FCSTD DOCUMENT  (FreeCAD 1.0R39319 (Git))
Label: Assy_Stack_Module_Tee_Cam
License: All rights reserved
LicenseURL: https://en.wikipedia.org/wiki/All_rights_reserved
objects: App::DocumentObjectGroup×3, App::Link×2, PartDesign::CoordinateSystem×1, App::FeaturePython×1, App::Part×1, TechDraw::DrawSVGTemplate×1, TechDraw::DrawProjGroupItem×1, TechDraw::DrawPage×1
note: 1 computed .brp shape members not serialized (recipe doc carries the construction recipe); baked Part::Feature solids carry a one-line shape summary decoded from their .brp
EXTERNAL_REF file=Assy_Stack_Module.FCStd obj=LCS_Origin
EXTERNAL_REF file=Assy_Stack_Module.FCStd obj=Assembly
EXTERNAL_REF file=Assy_Tee_Cam.FCStd obj=LCS_Origin
EXTERNAL_REF file=Assy_Tee_Cam.FCStd obj=Assembly

FEATURE [App::DocumentObjectGroup] Parts
FEATURE [PartDesign::CoordinateSystem] LCS_Origin
  AttacherType = Attacher::AttachEngine3D
  AttachmentSupport = -> [X_Axis]
  MapMode = 2
FEATURE [App::DocumentObjectGroup] Constraints
FEATURE [App::FeaturePython] Variables  # WARN: FeaturePython — macro-defined, semantics opaque (R4)
  Type = App::PropertyContainer
FEATURE [App::DocumentObjectGroup] Configurations
FEATURE [App::Link] Assy_Stack_Module
  AttachedBy = #LCS_Origin
  AttachedTo = Parent Assembly#LCS_Origin
  LinkedObject = -> <external Assy_Stack_Module.FCStd>#Assembly
  SolverId = Asm4EE
  expr: Placement = LCS_Origin.Placement * AttachmentOffset * Assy_Stack_Module#LCS_Origin.Placement ^ -1
FEATURE [App::Link] Assy_Tee_Cam
  AttachedBy = #LCS_Origin
  AttachedTo = Assy_Stack_Module#LCS_Origin
  AttachmentOffset = pos=(0,50,-41.75) rot=(-0.57735,0.57735,-0.57735;4.18879rad)
  LinkPlacement = pos=(0,50,-41.75) rot=(-0.57735,0.57735,-0.57735;4.18879rad)
  LinkedObject = -> <external Assy_Tee_Cam.FCStd>#Assembly
  Placement = pos=(0,50,-41.75) rot=(-0.57735,0.57735,-0.57735;4.18879rad)
  SolverId = Asm4EE
  expr: Placement = Assy_Stack_Module.Placement * Assy_Stack_Module#LCS_Origin.Placement * AttachmentOffset * Assy_Tee_Cam#LCS_Origin.Placement ^ -1
FEATURE [App::Part] Assembly  label="Assy_Stack_Module_Tee_Cam"
  AssemblyType = Part::Link
  Group = -> [LCS_Origin,Constraints,Variables,Configurations,Assy_Stack_Module,Assy_Tee_Cam]
  Origin = -> Origin
  Type = Assembly
FEATURE [TechDraw::DrawSVGTemplate] Template
  Height = 210
  Orientation = 1
  Template = C:/Program Files/FreeCAD 1.0/data/Mod/TechDraw/Templates/Default_Template_A4_Landscape.svg
  Width = 297
FEATURE [TechDraw::DrawProjGroupItem] View
  CoarseView = false
  Direction = (-0.57735,0.57735,-0.577351)
  Focus = 100
  HardHidden = false
  IsoCount = 0
  IsoHidden = false
  IsoVisible = false
  LockPosition = false
  Perspective = false
  Rotation = 0
  RotationVector = (1,0,0)
  ScaleType = 0
  ScrubCount = 1
  SeamHidden = false
  SeamVisible = false
  SmoothHidden = false
  SmoothVisible = true
  Source = -> [Assembly]
  Type = 0
  X = 148.5
  XDirection = (0.707107,0.707107,0)
  Y = 105
FEATURE [TechDraw::DrawPage] Page
  KeepUpdated = true
  NextBalloonIndex = 1
  ProjectionType = 0
  Template = -> Template
  Views = -> [View]

RESOLVED EXTERNAL PARTS (link-assembly join: the EXTERNAL_REF files above that resolve inside this repo's crawl, each included once):
---- part Assy_Stack_Module.FCStd = doc fcstd_b85c8f13e317 ----
FCSTD DOCUMENT  (FreeCAD 1.0R39319 (Git))
Label: Assy_Stack_Module
License: All rights reserved
LicenseURL: https://en.wikipedia.org/wiki/All_rights_reserved
objects: App::Link×5, Part::FeaturePython×4, App::DocumentObjectGroup×3, PartDesign::CoordinateSystem×1, App::FeaturePython×1, App::Part×1
note: 5 computed .brp shape members not serialized (recipe doc carries the construction recipe); baked Part::Feature solids carry a one-line shape summary decoded from their .brp
EXTERNAL_REF file=../../Part/Print/Stack_Module.FCStd obj=screen_ref
EXTERNAL_REF file=../../Part/Print/Stack_Module.FCStd obj=Part
EXTERNAL_REF file=../../Part/Print/Spacer.FCStd obj=LCS_1
EXTERNAL_REF file=../../Part/Print/Stack_Module.FCStd obj=spacer_att_1
EXTERNAL_REF file=../../Part/Print/Spacer.FCStd obj=Part
EXTERNAL_REF file=../../Part/Print/Stack_Module.FCStd obj=spacer_att_2
EXTERNAL_REF file=../../Part/Print/Stack_Module.FCStd obj=spacer_att_3
EXTERNAL_REF file=../../Part/Print/Stack_Module.FCStd obj=spacer_att_4

FEATURE [App::DocumentObjectGroup] Parts
FEATURE [PartDesign::CoordinateSystem] LCS_Origin
  AttacherType = Attacher::AttachEngine3D
  AttachmentSupport = -> [X_Axis]
  MapMode = 2
FEATURE [App::DocumentObjectGroup] Constraints
FEATURE [App::FeaturePython] Variables  # WARN: FeaturePython — macro-defined, semantics opaque (R4)
  Type = App::PropertyContainer
FEATURE [App::DocumentObjectGroup] Configurations
FEATURE [App::Link] Stack_Module
  AttachedBy = #screen_ref
  AttachedTo = Parent Assembly#LCS_Origin
  LinkPlacement = pos=(19.9856,50,3) rot=(0.57735,0.57735,0.57735;2.0944rad)
  LinkedObject = -> <external ../../Part/Print/Stack_Module.FCStd>#Part
  Placement = pos=(19.9856,50,3) rot=(0.57735,0.57735,0.57735;2.0944rad)
  SolverId = Asm4EE
  expr: Placement = LCS_Origin.Placement * AttachmentOffset * Stack_Module#screen_ref.Placement ^ -1
FEATURE [App::Link] Spacer
  AttachedBy = #LCS_1
  AttachedTo = Stack_Module#spacer_att_1
  LinkPlacement = pos=(-33.5144,116.5,-79.5) rot=(0.707107,0.707107,0;3.14159rad)
  LinkedObject = -> <external ../../Part/Print/Spacer.FCStd>#Part
  Placement = pos=(-33.5144,116.5,-79.5) rot=(0.707107,0.707107,0;3.14159rad)
  SolverId = Asm4EE
  expr: Placement = Stack_Module.Placement * Stack_Module#spacer_att_1.Placement * AttachmentOffset * Spacer#LCS_1.Placement ^ -1
FEATURE [App::Link] Spacer001
  AttachedBy = #LCS_1
  AttachedTo = Stack_Module#spacer_att_2
  LinkPlacement = pos=(82.4856,113.5,-79.5) rot=(0.707107,0.707107,0;3.14159rad)
  LinkedObject = -> <external ../../Part/Print/Spacer.FCStd>#Part
  Placement = pos=(82.4856,113.5,-79.5) rot=(0.707107,0.707107,0;3.14159rad)
  SolverId = Asm4EE
  expr: Placement = Stack_Module.Placement * Stack_Module#spacer_att_2.Placement * AttachmentOffset * Spacer#LCS_1.Placement ^ -1
FEATURE [App::Link] Spacer002
  AttachedBy = #LCS_1
  AttachedTo = Stack_Module#spacer_att_3
  AttachmentOffset = pos=(0,0,0) rot=(0,1,0;3.14159rad)
  LinkPlacement = pos=(-33.5144,-16.5,-79.5) rot=(0.707107,-0.707107,0;3.14159rad)
  LinkedObject = -> <external ../../Part/Print/Spacer.FCStd>#Part
  Placement = pos=(-33.5144,-16.5,-79.5) rot=(0.707107,-0.707107,0;3.14159rad)
  SolverId = Asm4EE
  expr: Placement = Stack_Module.Placement * Stack_Module#spacer_att_3.Placement * AttachmentOffset * Spacer#LCS_1.Placement ^ -1
FEATURE [App::Link] Spacer003
  AttachedBy = #LCS_1
  AttachedTo = Stack_Module#spacer_att_4
  AttachmentOffset = pos=(0,0,0) rot=(0,1,0;3.14159rad)
  LinkPlacement = pos=(82.4856,-13.5,-79.5) rot=(0.707107,-0.707107,0;3.14159rad)
  LinkedObject = -> <external ../../Part/Print/Spacer.FCStd>#Part
  Placement = pos=(82.4856,-13.5,-79.5) rot=(0.707107,-0.707107,0;3.14159rad)
  SolverId = Asm4EE
  expr: Placement = Stack_Module.Placement * Stack_Module#spacer_att_4.Placement * AttachmentOffset * Spacer#LCS_1.Placement ^ -1
FEATURE [Part::FeaturePython] Screw  label="M5x10-Screw"  # WARN: FeaturePython — macro-defined, semantics opaque (R4)
  BaseObject = -> Stack_Module [Body.Mirrored.Edge531]
  Diameter = 3
  Invert = true
  LeftHanded = false
  Length = 1
  LengthCustom = 10
  MatchOuter = false
  OffsetAngle = 0
  Placement = pos=(-31.0144,2.23e-14,-3) rot=(0.830469,-0.557065,0;3.14159rad)
  Thread = false
  Type = 86
FEATURE [Part::FeaturePython] Screw001  label="M5x10-Screw007"  # WARN: FeaturePython — macro-defined, semantics opaque (R4)
  BaseObject = -> Stack_Module [Body.Mirrored.Edge537]
  Diameter = 3
  Invert = true
  LeftHanded = false
  Length = 1
  LengthCustom = 10
  MatchOuter = false
  OffsetAngle = 0
  Placement = pos=(35.9856,8.1e-15,-3) rot=(0.830469,-0.557065,0;3.14159rad)
  Thread = false
  Type = 86
FEATURE [Part::FeaturePython] Screw002  label="M5x10-Screw008"  # WARN: FeaturePython — macro-defined, semantics opaque (R4)
  BaseObject = -> Stack_Module [Body.Mirrored.Edge265]
  Diameter = 3
  Invert = false
  LeftHanded = false
  Length = 1
  LengthCustom = 10
  MatchOuter = false
  OffsetAngle = 0
  Placement = pos=(35.9856,100,-3) rot=(-1,0,0;3.14159rad)
  Thread = false
  Type = 86
FEATURE [Part::FeaturePython] Screw003  label="M5x10-Screw009"  # WARN: FeaturePython — macro-defined, semantics opaque (R4)
  BaseObject = -> Stack_Module [Body.Mirrored.Edge258]
  Diameter = 3
  Invert = false
  LeftHanded = false
  Length = 1
  LengthCustom = 10
  MatchOuter = false
  OffsetAngle = 0
  Placement = pos=(-31.0144,100,-3) rot=(-1,0,0;3.14159rad)
  Thread = false
  Type = 86
FEATURE [App::Part] Assembly  label="Assy_Stack_Module"
  AssemblyType = Part::Link
  Group = -> [LCS_Origin,Constraints,Variables,Configurations,Stack_Module,Spacer,Spacer001,Spacer002,Spacer003,Screw,Screw001,Screw002,Screw003]
  Origin = -> Origin
  Type = Assembly
---- part Assy_Tee_Cam.FCStd = doc fcstd_2765aa89e358 ----
FCSTD DOCUMENT  (FreeCAD 1.0R39319 (Git))
Label: Assy_Tee_Cam
License: All rights reserved
LicenseURL: https://en.wikipedia.org/wiki/All_rights_reserved
objects: App::DocumentObjectGroup×3, App::Link×3, PartDesign::CoordinateSystem×1, App::FeaturePython×1, App::Part×1
note: 1 computed .brp shape members not serialized (recipe doc carries the construction recipe); baked Part::Feature solids carry a one-line shape summary decoded from their .brp
EXTERNAL_REF file=Assy_Camera_Eyeball.FCStd obj=LCS_Origin
EXTERNAL_REF file=Assy_Camera_Eyeball.FCStd obj=Assembly
EXTERNAL_REF file=Assy_EyeScreen.FCStd obj=LCS_Origin
EXTERNAL_REF file=Assy_EyeScreen.FCStd obj=Assembly
EXTERNAL_REF file=Assy_EyeScreen_Clamp.FCStd obj=LCS_Origin
EXTERNAL_REF file=Assy_EyeScreen_Clamp.FCStd obj=Assembly

FEATURE [App::DocumentObjectGroup] Parts
FEATURE [PartDesign::CoordinateSystem] LCS_Origin
  AttacherType = Attacher::AttachEngine3D
  AttachmentSupport = -> [X_Axis]
  MapMode = 2
FEATURE [App::DocumentObjectGroup] Constraints
FEATURE [App::FeaturePython] Variables  # WARN: FeaturePython — macro-defined, semantics opaque (R4)
  Type = App::PropertyContainer
FEATURE [App::DocumentObjectGroup] Configurations
FEATURE [App::Link] Assy_Camera_Eyeball
  AttachedBy = #LCS_Origin
  AttachedTo = Parent Assembly#LCS_Origin
  LinkedObject = -> <external Assy_Camera_Eyeball.FCStd>#Assembly
  SolverId = Asm4EE
  expr: Placement = LCS_Origin.Placement * AttachmentOffset * Assy_Camera_Eyeball#LCS_Origin.Placement ^ -1
FEATURE [App::Link] Assy_EyeScreen
  AttachedBy = #LCS_Origin
  AttachedTo = Parent Assembly#LCS_Origin
  AttachmentOffset = pos=(0,0,0) rot=(0.57735,0.57735,-0.57735;4.18879rad)
  LinkPlacement = pos=(0,0,0) rot=(0.57735,0.57735,-0.57735;4.18879rad)
  LinkedObject = -> <external Assy_EyeScreen.FCStd>#Assembly
  Placement = pos=(0,0,0) rot=(0.57735,0.57735,-0.57735;4.18879rad)
  SolverId = Asm4EE
  expr: Placement = LCS_Origin.Placement * AttachmentOffset * Assy_EyeScreen#LCS_Origin.Placement ^ -1
FEATURE [App::Link] Assy_EyeScreen_Clamp
  AttachedBy = #LCS_Origin
  AttachedTo = Parent Assembly#LCS_Origin
  AttachmentOffset = pos=(0,0,0) rot=(-0.57735,-0.57735,0.57735;4.18879rad)
  LinkPlacement = pos=(0,0,0) rot=(-0.57735,-0.57735,0.57735;4.18879rad)
  LinkedObject = -> <external Assy_EyeScreen_Clamp.FCStd>#Assembly
  Placement = pos=(0,0,0) rot=(-0.57735,-0.57735,0.57735;4.18879rad)
  SolverId = Asm4EE
  expr: Placement = LCS_Origin.Placement * AttachmentOffset * Assy_EyeScreen_Clamp#LCS_Origin.Placement ^ -1
FEATURE [App::Part] Assembly  label="Assy_Tee_Cam"
  AssemblyType = Part::Link
  Group = -> [LCS_Origin,Constraints,Variables,Configurations,Assy_Camera_Eyeball,Assy_EyeScreen,Assy_EyeScreen_Clamp]
  Origin = -> Origin
  Type = Assembly
